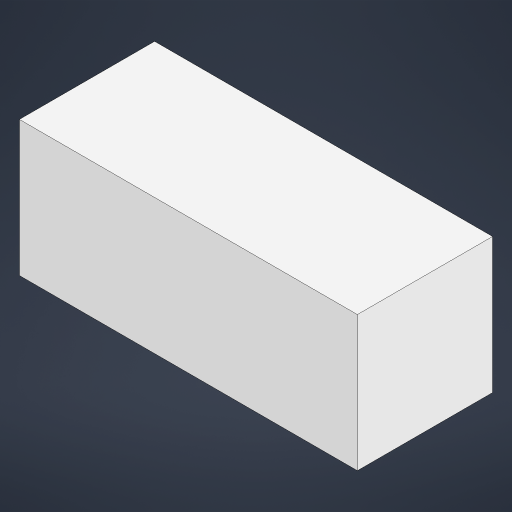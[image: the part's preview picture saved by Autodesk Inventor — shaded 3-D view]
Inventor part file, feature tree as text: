
AUTODESK INVENTOR PART (.ipt)
format: ipt  version: 2023.1 (Build 271208000, 208)  size: 152,576 bytes
history: native  units: in
note: dims shown in document units (in); Inventor stores cm internally (conversion verified against a paired STEP export)
features: extrude x1, sketch x1
ambient origin geometry x8: Origin, YZ Plane, XZ Plane, XY Plane, X Axis, Y Axis, Z Axis, Center Point
bodies: Solid1 (feature_tree)
feature tree (2):
  extrude  "Extrusion1"  Depth=4.0in
  sketch  "Sketch1"  dims[d0=10.0in d1=4.0in d2=4.0in d3=0.0in]
